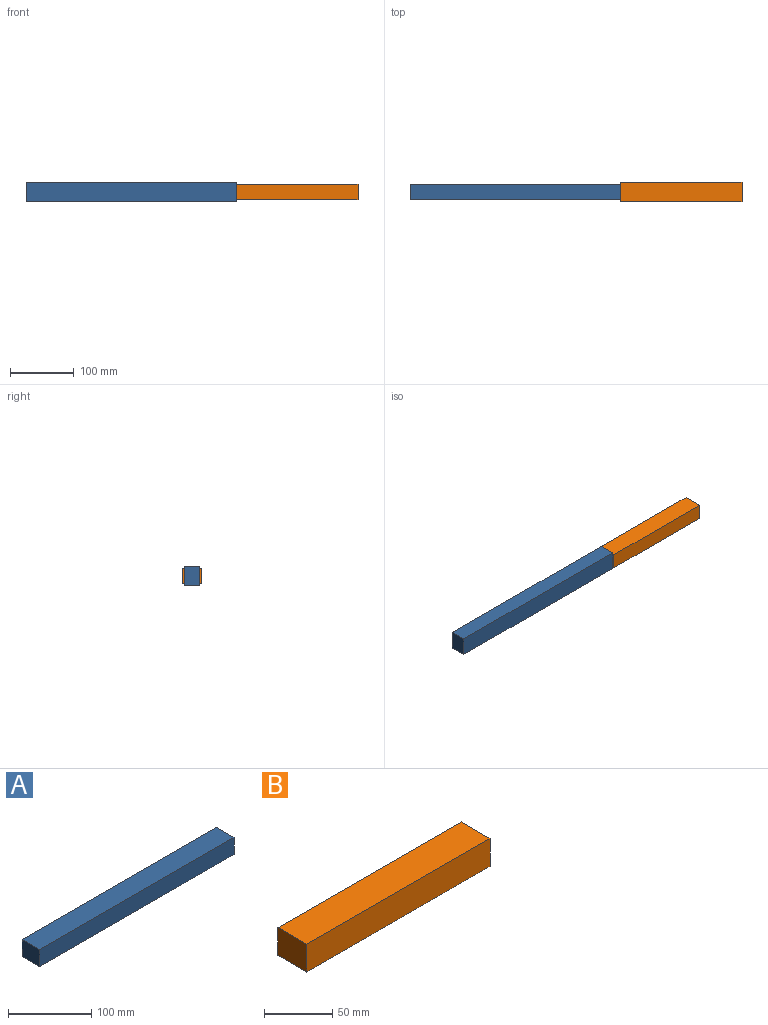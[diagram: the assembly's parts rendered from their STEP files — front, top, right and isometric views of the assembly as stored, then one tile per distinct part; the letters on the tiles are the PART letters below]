
ASSEMBLY  parts=2 mates=1
PART A: 6 faces, bbox 330x30x25 mm
  f0: plane 330x25mm, normal (0,1,0), area 8250mm2, adj f1,f3,f4,f5
  f1: plane 30x25mm, normal (-1,0,0), area 750mm2, adj f0,f2,f4,f5
  f2: plane 330x25mm, normal (0,-1,0), area 8250mm2, adj f1,f3,f4,f5
  f3: plane 30x25mm, normal (1,0,0), area 750mm2, adj f0,f2,f4,f5
  f4: plane 330x30mm, normal (0,0,1), area 9900mm2, adj f0,f1,f2,f3
  f5: plane 330x30mm, normal (0,0,-1), area 9900mm2, adj f0,f1,f2,f3
PART B: 6 faces, bbox 190x30x25 mm
  f0: plane 190x25mm, normal (0,1,0), area 4750mm2, adj f1,f3,f4,f5
  f1: plane 30x25mm, normal (-1,0,0), area 750mm2, adj f0,f2,f4,f5
  f2: plane 190x25mm, normal (0,-1,0), area 4750mm2, adj f1,f3,f4,f5
  f3: plane 30x25mm, normal (1,0,0), area 750mm2, adj f0,f2,f4,f5
  f4: plane 190x30mm, normal (0,0,1), area 5700mm2, adj f0,f1,f2,f3
  f5: plane 190x30mm, normal (0,0,-1), area 5700mm2, adj f0,f1,f2,f3
PLACE A rot(axis=(-1,0,0),90deg) t=(-402.85,-116.08,42.9)mm
PLACE B rot(axis=(0,-1,0),180deg) t=(-144.41,-103.98,81.21)mm
MATE ball A.f3 <-> B.f3  axis (1,0,0) through (-229.76,-103.58,68.71)mm
